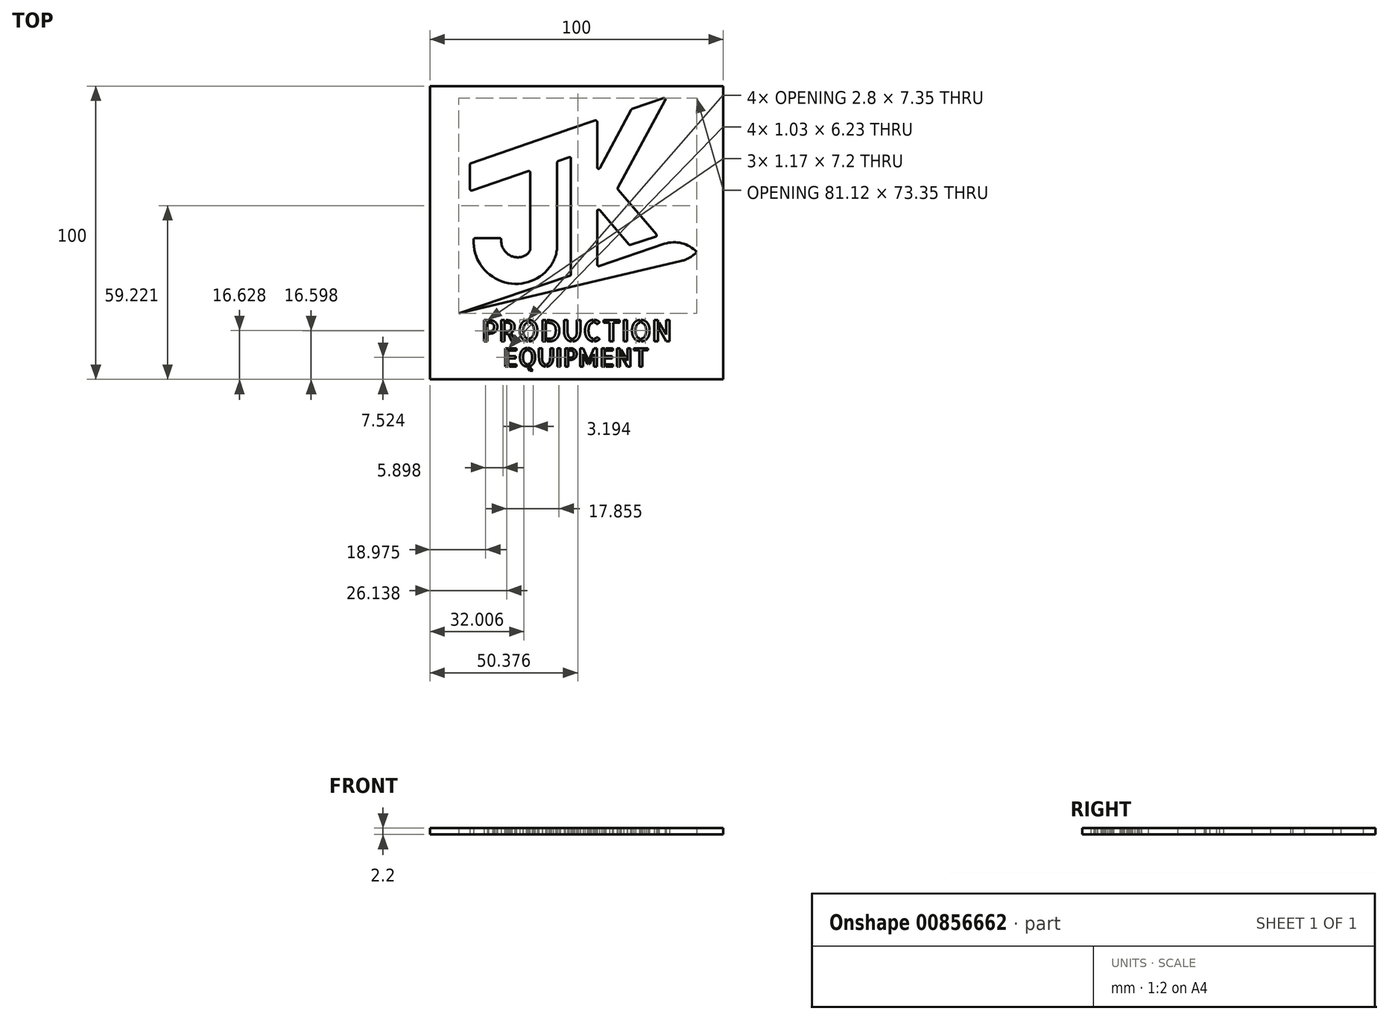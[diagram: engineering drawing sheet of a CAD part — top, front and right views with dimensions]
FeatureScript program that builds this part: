
annotation { "Feature Type Name" : "Feature", "Feature Type Description" : "" }
export const myFeature = defineFeature(function(context is Context, id is Id, definition is map)
    precondition{}
    {
        {
            var Q0;
            Q0=qCreatedBy(makeId("Top.planeOp"),FACE);
            var sketch = newSketch(context, id + "F0", { "sketchPlane" : qUnion([Q0])});
            skLineSegment(sketch, "E0.bottom", {"start": v(-55.7, 40.56) * mm, "end": v(44.3, 40.56) * mm});
            skLineSegment(sketch, "E0.top", {"start": v(-55.7, -59.44) * mm, "end": v(44.3, -59.44) * mm});
            skLineSegment(sketch, "E0.left", {"start": v(-55.7, 40.56) * mm, "end": v(-55.7, -59.44) * mm});
            skLineSegment(sketch, "E0.right", {"start": v(44.3, 40.56) * mm, "end": v(44.3, -59.44) * mm});
            skLineSegment(sketch, "E1", {"start": v(-42.06, 14.17) * mm, "end": v(-12.33, 24.38) * mm});
            skLineSegment(sketch, "E2", {"start": v(-12.33, 24.38) * mm, "end": v(-12.33, -15.81) * mm});
            skLineSegment(sketch, "E3", {"start": v(-42.06, 14.17) * mm, "end": v(-42.06, 4.72) * mm});
            skLineSegment(sketch, "E4", {"start": v(-42.06, 4.72) * mm, "end": v(-12.33, 14.93) * mm});
            skLineSegment(sketch, "E5", {"start": v(-21.49, 11.79) * mm, "end": v(-21.49, -15.81) * mm});
            skLineSegment(sketch, "E6", {"start": v(-31.35, -11.28) * mm, "end": v(-40.8, -11.28) * mm});
            skArc(sketch, "E7", {"start": v(-31.35, -11.28) * mm, "mid": v(-28.15, -17.3) * mm, "end": v(-21.49, -15.81) * mm});
            skArc(sketch, "E8", {"start": v(-40.8, -11.28) * mm, "mid": v(-28.66, -26.66) * mm, "end": v(-12.33, -15.81) * mm});
            skLineSegment(sketch, "E9", {"start": v(-7.67, 26.02) * mm, "end": v(1.28, 29.04) * mm});
            skLineSegment(sketch, "E10", {"start": v(-7.67, 26.02) * mm, "end": v(-7.67, -26.31) * mm});
            skLineSegment(sketch, "E11", {"start": v(1.28, 29.04) * mm, "end": v(1.28, -23.29) * mm});
            skLineSegment(sketch, "E12", {"start": v(1.28, -23.29) * mm, "end": v(-7.67, -26.31) * mm});
            skLineSegment(sketch, "E13", {"start": v(1.28, 10.9) * mm, "end": v(13, 32.7) * mm});
            skLineSegment(sketch, "E14", {"start": v(13, 32.7) * mm, "end": v(22.2, 35.85) * mm});
            skLineSegment(sketch, "E15", {"start": v(6.7, 7.26) * mm, "end": v(21.94, -10.52) * mm});
            skLineSegment(sketch, "E16", {"start": v(21.94, -10.52) * mm, "end": v(12.37, -13.67) * mm});
            skLineSegment(sketch, "E17", {"start": v(12.37, -13.67) * mm, "end": v(1.95, -1.5) * mm});
            skLineSegment(sketch, "E18", {"start": v(-12.33, 24.38) * mm, "end": v(-7.67, 26.02) * mm});
            skLineSegment(sketch, "E19", {"start": v(-12.33, 14.93) * mm, "end": v(-4.4, 17.7) * mm});
            skLineSegment(sketch, "E20", {"start": v(22.2, 35.85) * mm, "end": v(25.1, 36.84) * mm});
            skLineSegment(sketch, "E21", {"start": v(25.1, 36.84) * mm, "end": v(8.15, 5.56) * mm});
            skLineSegment(sketch, "E22", {"start": v(1.95, -1.5) * mm, "end": v(-1, 1.4) * mm});
            skLineSegment(sketch, "E23", {"start": v(38.07, -8.55) * mm, "end": v(-45.89, -36.9) * mm});
            skLineSegment(sketch, "E24", {"start": v(38.07, -8.55) * mm, "end": v(38.07, -17.13) * mm});
            skLineSegment(sketch, "E25", {"start": v(-45.89, -36.9) * mm, "end": v(38.07, -17.13) * mm});
            skLineSegment(sketch, "E26", {"start": v(-28.15, -17.3) * mm, "end": v(-40.8, -11.28) * mm});
            skText(sketch, "E27", { "text": "PRODUCTION", "fontName": "AllertaStencil-Regular.ttf"});
            skText(sketch, "E28", { "text": "EQUIPMENT", "fontName": "AllertaStencil-Regular.ttf"});
            const initialGuessF0  = {"E27": [-0.0382, -0.04644, 1, 0, 0.0072], "E28": [-0.03088, -0.05503, 1, 0, 0.00623]};
            skSetInitialGuess(sketch, initialGuessF0);
            skSolve(sketch);
        }
        {
            var Q0;
            Q0=makeQuery(id+"F0.imprint","IMPRINT",FACE,{"disambiguationData":[TD([[makeQuery(id+"F0.imprint","IMPRINT",EDGE,{"derivedFrom":sQuery(id+"F0.wireOp",EDGE,"E0.bottom")}),-1.0]])]});
            extrude(context, id + "F1", {"entities" : qUnion([Q0]), "depth" : 2.2 * mm, "offsetDistance" : 25 * mm});
        }
        {
            var Q0;
            Q0=makeQuery(id+"F1.opExtrude","SWEPT_EDGE",EDGE,{"disambiguationData":[OSD([sQuery(id+"F0.wireOp",EDGE,"E9"),sQuery(id+"F0.wireOp",EDGE,"E11")])]});
            var Q1;
            Q1=makeQuery(id+"F1.opExtrude","SWEPT_EDGE",EDGE,{"disambiguationData":[OSD([sQuery(id+"F0.wireOp",EDGE,"E13"),sQuery(id+"F0.wireOp",EDGE,"E14")])]});
            var Q2;
            Q2=makeQuery(id+"F1.opExtrude","SWEPT_EDGE",EDGE,{"disambiguationData":[OSD([sQuery(id+"F0.wireOp",EDGE,"E20"),sQuery(id+"F0.wireOp",EDGE,"E21")])]});
            var Q3;
            Q3=makeQuery(id+"F1.opExtrude","SWEPT_EDGE",EDGE,{"disambiguationData":[OSD([sQuery(id+"F0.wireOp",EDGE,"E15"),sQuery(id+"F0.wireOp",EDGE,"E21")])]});
            var Q4;
            Q4=makeQuery(id+"F1.opExtrude","SWEPT_EDGE",EDGE,{"disambiguationData":[OSD([sQuery(id+"F0.wireOp",EDGE,"E1"),sQuery(id+"F0.wireOp",EDGE,"E3")])]});
            var Q5;
            Q5=makeQuery(id+"F1.opExtrude","SWEPT_EDGE",EDGE,{"disambiguationData":[OSD([sQuery(id+"F0.wireOp",EDGE,"E3"),sQuery(id+"F0.wireOp",EDGE,"E4")])]});
            var Q6;
            Q6=makeQuery(id+"F1.opExtrude","SWEPT_EDGE",EDGE,{"disambiguationData":[OSD([sQuery(id+"F0.wireOp",EDGE,"E4"),sQuery(id+"F0.wireOp",EDGE,"E5")])]});
            var Q7;
            Q7=makeQuery(id+"F1.opExtrude","SWEPT_EDGE",EDGE,{"disambiguationData":[OSD([sQuery(id+"F0.wireOp",EDGE,"E6"),sQuery(id+"F0.wireOp",EDGE,"E8")])]});
            var Q8;
            Q8=makeQuery(id+"F1.opExtrude","SWEPT_EDGE",EDGE,{"disambiguationData":[OSD([sQuery(id+"F0.wireOp",EDGE,"E6"),sQuery(id+"F0.wireOp",EDGE,"E7")])]});
            var Q9;
            Q9=makeQuery(id+"F1.opExtrude","SWEPT_EDGE",EDGE,{"disambiguationData":[OSD([sQuery(id+"F0.wireOp",EDGE,"E2"),sQuery(id+"F0.wireOp",EDGE,"E4"),sQuery(id+"F0.wireOp",EDGE,"E19")])]});
            var Q10;
            Q10=makeQuery(id+"F1.opExtrude","SWEPT_EDGE",EDGE,{"disambiguationData":[OSD([sQuery(id+"F0.wireOp",EDGE,"E10"),sQuery(id+"F0.wireOp",EDGE,"E19")])]});
            var Q11;
            Q11=makeQuery(id+"F1.opExtrude","SWEPT_EDGE",EDGE,{"disambiguationData":[OSD([sQuery(id+"F0.wireOp",EDGE,"E10"),sQuery(id+"F0.wireOp",EDGE,"E12")])]});
            var Q12;
            Q12=makeQuery(id+"F1.opExtrude","SWEPT_EDGE",EDGE,{"disambiguationData":[OSD([sQuery(id+"F0.wireOp",EDGE,"E11"),sQuery(id+"F0.wireOp",EDGE,"E12")])]});
            var Q13;
            Q13=makeQuery(id+"F1.opExtrude","SWEPT_EDGE",EDGE,{"disambiguationData":[OSD([sQuery(id+"F0.wireOp",EDGE,"E16"),sQuery(id+"F0.wireOp",EDGE,"E17")])]});
            var Q14;
            Q14=makeQuery(id+"F1.opExtrude","SWEPT_EDGE",EDGE,{"disambiguationData":[OSD([sQuery(id+"F0.wireOp",EDGE,"E15"),sQuery(id+"F0.wireOp",EDGE,"E16")])]});
            fillet(context, id + "F2", {"entities" : qUnion([Q0, Q1, Q2, Q3, Q4, Q5, Q6, Q7, Q8, Q9, Q10, Q11, Q12, Q13, Q14]), "radius" : 0.5 * mm, "tangentPropagation" : true, "allowEdgeOverflow" : false});
        }
        {
            var Q0;
            Q0=makeQuery(id+"F1.opExtrude","SWEPT_EDGE",EDGE,{"disambiguationData":[OSD([sQuery(id+"F0.wireOp",EDGE,"E5"),sQuery(id+"F0.wireOp",EDGE,"E7")])]});
            fillet(context, id + "F3", {"entities" : qUnion([Q0]), "radius" : 3.1 * mm, "tangentPropagation" : true, "allowEdgeOverflow" : false});
        }
        {
            var Q0;
            Q0=makeQuery(id+"F1.opExtrude","SWEPT_EDGE",EDGE,{"disambiguationData":[OSD([sQuery(id+"F0.wireOp",EDGE,"E2"),sQuery(id+"F0.wireOp",EDGE,"E8")])]});
            fillet(context, id + "F4", {"entities" : qUnion([Q0]), "radius" : 12.45 * mm, "tangentPropagation" : true, "allowEdgeOverflow" : false});
        }
        {
            var Q0;
            Q0=makeQuery(id+"F1.opExtrude","SWEPT_EDGE",EDGE,{"disambiguationData":[OSD([sQuery(id+"F0.wireOp",EDGE,"E24"),sQuery(id+"F0.wireOp",EDGE,"E25")])]});
            var Q1;
            Q1=makeQuery(id+"F1.opExtrude","SWEPT_EDGE",EDGE,{"disambiguationData":[OSD([sQuery(id+"F0.wireOp",EDGE,"E23"),sQuery(id+"F0.wireOp",EDGE,"E24")])]});
            fillet(context, id + "F5", {"entities" : qUnion([Q0, Q1]), "radius" : 10.5 * mm, "tangentPropagation" : true, "allowEdgeOverflow" : false});
        }
    });
